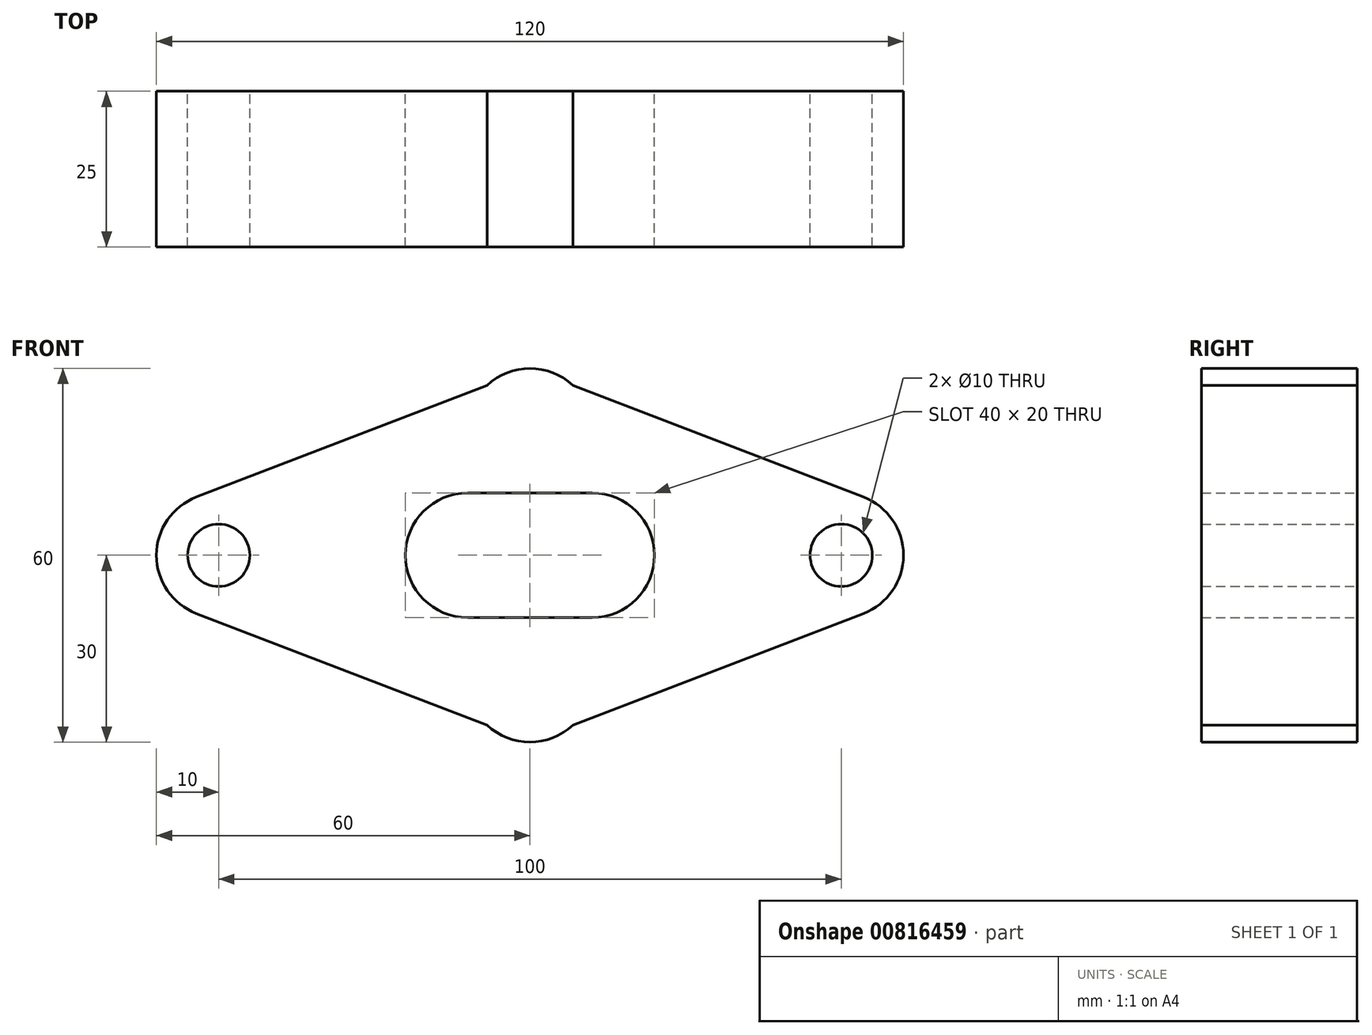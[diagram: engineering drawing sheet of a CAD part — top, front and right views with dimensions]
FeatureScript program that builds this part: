
annotation { "Feature Type Name" : "Feature", "Feature Type Description" : "" }
export const myFeature = defineFeature(function(context is Context, id is Id, definition is map)
    precondition{}
    {
        {
            var Q0;
            Q0=qCreatedBy(makeId("Front.planeOp"),FACE);
            var sketch = newSketch(context, id + "F0", { "sketchPlane" : qUnion([Q0])});
            skArc(sketch, "E0.MirrorC", {"start": v(10, 10) * mm, "mid": v(20, 0) * mm, "end": v(10, -10) * mm});
            skCircle(sketch, "E1", {"center": v(-50, 0) * mm, "radius": 10 * mm});
            skCircle(sketch, "E2", {"center": v(50, 0) * mm, "radius": 10 * mm});
            skCircle(sketch, "E3", {"center": v(-50, 0) * mm, "radius": 5 * mm});
            skCircle(sketch, "E4", {"center": v(50, 0) * mm, "radius": 5 * mm});
            skArc(sketch, "E5", {"start": v(-0.22, 10) * mm, "mid": v(0, 10) * mm, "end": v(0.22, 10) * mm});
            skArc(sketch, "E6", {"start": v(-6.9, -27.24) * mm, "mid": v(0, -30) * mm, "end": v(6.9, -27.24) * mm});
            skArc(sketch, "E7", {"start": v(-10, 10) * mm, "mid": v(-20, 0) * mm, "end": v(-10, -10) * mm});
            skLineSegment(sketch, "E8", {"start": v(-10, -10) * mm, "end": v(10, -10) * mm});
            skLineSegment(sketch, "E9", {"start": v(10, 10) * mm, "end": v(-10, 10) * mm});
            skLineSegment(sketch, "E10", {"start": v(-53.58, -9.34) * mm, "end": v(-6.9, -27.24) * mm});
            skLineSegment(sketch, "E11", {"start": v(53.58, 9.34) * mm, "end": v(6.9, 27.24) * mm});
            skLineSegment(sketch, "E12", {"start": v(-6.9, 27.24) * mm, "end": v(-53.58, 9.34) * mm});
            skLineSegment(sketch, "E13", {"start": v(6.9, -27.24) * mm, "end": v(53.58, -9.34) * mm});
            skArc(sketch, "E14.trimOffspring", {"start": v(6.9, 27.24) * mm, "mid": v(0, 30) * mm, "end": v(-6.9, 27.24) * mm});
            skSolve(sketch);
        }
        {
            var Q0;
            Q0 = qSketchRegion(id + "F0", true);
            extrude(context, id + "F1", {"entities" : qUnion([Q0]), "depth" : 25 * mm, "offsetDistance" : 25 * mm});
        }
    });
